# Revit family: Hager-Type B SP&N Distribution Boards-Surface_mounted-IP3X-With_Cover-NoHosted-GB-en
name_source: partatom
category: Electrical Equipment
units: mm (PartAtom-declared; Revit-internal decimal feet)

## family parameters
Always vertical = Yes
Cut with Voids When Loaded = No
Maintain Annotation Orientation = No
Panel Configuration = Two Columns, Circuits Across
Part Type = Panelboard
Room Calculation Point = No
Round Connector Dimension = Use Diameter
Shared = No
Work Plane-Based = Yes

## types (42) — shared parameters
BC_MODEL_ID = 1554493
BC_OBJECT_ID = 513945
BC_OBJECT_VERSION = #1
Classification.Uniclass.Pr.Description = Control circuit device enclosures
Classification.Uniclass.Pr.Number = Pr_80_77_28_16
Code hager = ADD-EC000214_UKVR
Default Elevation = 1219 mm
EF000003 - Mounting method = Surface mounted
EF000007 - Colour = Grey
EF000008 - Width = 465 mm  [stored 1.52559 ft]
EF000024 - UV resistant = No
EF000116 - RAL number = 7035
EF000118 - With mounting plate = No
EF000218 - Built-in depth = 150 mm
EF000332 - Built-in height = 450 mm  [stored 1.47638 ft]
EF000846 - Built-in width = 350 mm  [stored 1.14829 ft]
EF001062 - EMC-version = No
EF001088 - Extension possible = Yes
EF001134 - DIN-rail = Yes
EF001134 - With DIN-rail = No
EF001596 - Housing material = Steel
EF005474 - Degree of protection (IP rating) = IP3X
EF006306 - With lock = Yes
EF015776 - Earthing terminal block = Yes
EF015777 - Neutral terminal block = Yes
EF015941 - Signal passing door = No
ETIM class code = EC000214
ETIM class name = Small distribution board
HG000002-With door or cover = Yes
HG000003-Range = Type B SP&N Distribution Boards
HG000005-Thickness = 3 mm  [stored 0.00984252 ft]
HG000006-Flush mounted = No
HG000017-Distance between poles = 18 mm  [stored 0.0590551 ft]
HG000060-RAL-number = 7035
HG000099-Onfly Template ID = 507572
Manufacturer = Hager
Name = Type B SP&N Distribution Boards-Surface_mounted-IP3X-With_Cover-GB
Name BIM&CO = Electricity
Name hager = ADD_Enclosures_EC000214
Type Comments = Type B SP&N Distribution Boards
Uniformat = Low Tension Service & Dist.
Uniformat code = D501001
zero-valued in all types: EF000218 - Recess depth, EF000266 - Number of rows, EF000332 - Recess height, EF000846 - Recess width, EF001131 - Internal depth

## per-type parameters (varying)
| type | BC_VARIANT_ID | EF000040 - Height | EF000049 - Depth | EF002950 - Width in number of modular spacings | EF006244 - Transparent cover/door | HG000004-Manufacturer reference | HGEF000266-Number of rows | HGEF002950-Width in number of modular spacings | Model |
| Type B SP&N Distribution Boards-Surface_mounted_W465_H500_D132_6_Modular_Spacing-JK104B | 1179296 | 500 mm  [stored 1.64042 ft] | 132 mm  [stored 0.433071 ft] | 6 | No | JK104B | 0 | 8 | JK104B |
| Type B SP&N Distribution Boards-Surface_mounted_W465_H500_D132_6_Modular_Spacing-JK104BA3 | 1179297 | 500 mm  [stored 1.64042 ft] | 132 mm  [stored 0.433071 ft] | 6 | No | JK104BA3 | 0 | 12 | JK104BA3 |
| Type B SP&N Distribution Boards-Surface_mounted_W465_H500_D132_6_Modular_Spacing-JK104BG | 1179298 | 500 mm  [stored 1.64042 ft] | 132 mm  [stored 0.433071 ft] | 6 | Yes | JK104BG | 0 | 16 | JK104BG |
| Type B SP&N Distribution Boards-Surface_mounted_W465_H550_D132_9_Modular_Spacing-JK106B | 1179299 | 550 mm | 132 mm  [stored 0.433071 ft] | 9 | Yes | JK106B | 0 | 22 | JK106B |
| Type B SP&N Distribution Boards-Surface_mounted_W465_H550_D132_9_Modular_Spacing-JK106BA3 | 1179300 | 550 mm | 132 mm  [stored 0.433071 ft] | 9 | No | JK106BA3 | 0 | 12 | JK106BA3 |
| Type B SP&N Distribution Boards-Surface_mounted_W465_H550_D132_9_Modular_Spacing-JK106BG | 1179301 | 550 mm | 132 mm  [stored 0.433071 ft] | 9 | Yes | JK106BG | 0 | 16 | JK106BG |
| Type B SP&N Distribution Boards-Surface_mounted_W465_H625_D132_12_Modular_Spacing-JK108B | 1179302 | 625 mm  [stored 2.05052 ft] | 132 mm  [stored 0.433071 ft] | 12 | No | JK108B | 0 | 22 | JK108B |
| Type B SP&N Distribution Boards-Surface_mounted_W465_H625_D132_12_Modular_Spacing-JK108BA3 | 1179303 | 625 mm  [stored 2.05052 ft] | 132 mm  [stored 0.433071 ft] | 12 | No | JK108BA3 | 0 | 22 | JK108BA3 |
| Type B SP&N Distribution Boards-Surface_mounted_W465_H625_D132_12_Modular_Spacing-JK108BG | 1179304 | 625 mm  [stored 2.05052 ft] | 132 mm  [stored 0.433071 ft] | 12 | Yes | JK108BG | 0 | 16 | JK108BG |
| Type B SP&N Distribution Boards-Surface_mounted_W465_H850_D132_18_Modular_Spacing-JK112B | 1179305 | 850 mm  [stored 2.78871 ft] | 132 mm  [stored 0.433071 ft] | 18 | No | JK112B | 0 | 22 | JK112B |
| Type B SP&N Distribution Boards-Surface_mounted_W465_H850_D132_18_Modular_Spacing-JK112BA3 | 1179306 | 850 mm  [stored 2.78871 ft] | 132 mm  [stored 0.433071 ft] | 18 | No | JK112BA3 | 0 | 22 | JK112BA3 |
| Type B SP&N Distribution Boards-Surface_mounted_W465_H850_D132_18_Modular_Spacing-JK112BG | 1179307 | 850 mm  [stored 2.78871 ft] | 132 mm  [stored 0.433071 ft] | 18 | Yes | JK112BG | 1 | 16 | JK112BG |
| Type B SP&N Distribution Boards-Surface_mounted_W465_H950_D132_24_Modular_Spacing-JK116B | 1179308 | 950 mm  [stored 3.1168 ft] | 132 mm  [stored 0.433071 ft] | 24 | No | JK116B | 0 | 0 | JK116B |
| Type B SP&N Distribution Boards-Surface_mounted_W465_H950_D132_24_Modular_Spacing-JK116BA3 | 1179309 | 950 mm  [stored 3.1168 ft] | 132 mm  [stored 0.433071 ft] | 24 | No | JK116BA3 | 0 | 0 | JK116BA3 |
| Type B SP&N Distribution Boards-Surface_mounted_W465_H950_D132_24_Modular_Spacing-JK116BG | 1179310 | 950 mm  [stored 3.1168 ft] | 132 mm  [stored 0.433071 ft] | 24 | Yes | JK116BG | 0 | 0 | JK116BG |
| Type B SP&N Distribution Boards-Surface_mounted_W465_H1100_D165_27_Modular_Spacing-JK118B | 1179311 | 1100 mm | 165 mm | 27 | No | JK118B | 0 | 0 | JK118B |
| Type B SP&N Distribution Boards-Surface_mounted_W465_H1100_D165_27_Modular_Spacing-JK118BA3 | 1179312 | 1100 mm | 165 mm | 27 | No | JK118BA3 | 0 | 0 | JK118BA3 |
| Type B SP&N Distribution Boards-Surface_mounted_W465_H1100_D165_27_Modular_Spacing-JK118BG | 1179313 | 1100 mm | 165 mm | 27 | Yes | JK118BG | 0 | 0 | JK118BG |
| Type B SP&N Distribution Boards-Surface_mounted_W465_H1250_D165_36_Modular_Spacing-JK124B | 1179314 | 1250 mm  [stored 4.10105 ft] | 165 mm | 36 | No | JK124B | 1 | 16 | JK124B |
| Type B SP&N Distribution Boards-Surface_mounted_W465_H1250_D165_36_Modular_Spacing-JK124BA3 | 1179315 | 1250 mm  [stored 4.10105 ft] | 165 mm | 36 | No | JK124BA3 | 1 | 16 | JK124BA3 |
| Type B SP&N Distribution Boards-Surface_mounted_W465_H1250_D165_36_Modular_Spacing-JK124BG | 1179316 | 1250 mm  [stored 4.10105 ft] | 165 mm | 36 | Yes | JK124BG | 2 | 16 | JK124BG |
| Type B SP&N Distribution Boards-Surface_mounted_W465_H1250_D165_18_Modular_Spacing-JK20210B | 1179317 | 1250 mm  [stored 4.10105 ft] | 165 mm | 18 | No | JK20210B | 2 | 16 | JK20210B |
| Type B SP&N Distribution Boards-Surface_mounted_W465_H1250_D165_18_Modular_Spacing-JK20210BG | 1179318 | 1250 mm  [stored 4.10105 ft] | 165 mm | 18 | Yes | JK20210BG | 2 | 16 | JK20210BG |
| Type B SP&N Distribution Boards-Surface_mounted_W465_H1400_D165_27_Modular_Spacing-JK20216B | 1179319 | 1400 mm  [stored 4.59318 ft] | 165 mm | 27 | No | JK20216B | 2 | 16 | JK20216B |
| Type B SP&N Distribution Boards-Surface_mounted_W465_H1400_D165_27_Modular_Spacing-JK20216BG | 1179320 | 1400 mm  [stored 4.59318 ft] | 165 mm | 27 | Yes | JK20216BG | 2 | 16 | JK20216BG |
| Type B SP&N Distribution Boards-Surface_mounted_W465_H1400_D165_33_Modular_Spacing-JK20220B | 1179321 | 1400 mm  [stored 4.59318 ft] | 165 mm | 33 | No | JK20220B | 2 | 16 | JK20220B |
| Type B SP&N Distribution Boards-Surface_mounted_W465_H1400_D165_33_Modular_Spacing-JK20220BG | 1179322 | 1400 mm  [stored 4.59318 ft] | 165 mm | 33 | Yes | JK20220BG | 3 | 16 | JK20220BG |
| Type B SP&N Distribution Boards-Surface_mounted_W465_H950_D166_12_Modular_Spacing-JK208B | 1179323 | 950 mm  [stored 3.1168 ft] | 166 mm  [stored 0.544619 ft] | 12 | No | JK208B | 3 | 16 | JK208B |
| Type B SP&N Distribution Boards-Surface_mounted_W465_H950_D165_12_Modular_Spacing-JK208BA3 | 1179324 | 950 mm  [stored 3.1168 ft] | 165 mm | 12 | No | JK208BA3 | 4 | 16 | JK208BA3 |
| Type B SP&N Distribution Boards-Surface_mounted_W465_H950_D165_12_Modular_Spacing-JK208BG | 1179325 | 950 mm  [stored 3.1168 ft] | 165 mm | 12 | Yes | JK208BG | 4 | 16 | JK208BG |
| Type B SP&N Distribution Boards-Surface_mounted_W465_H1100_D165_18_Modular_Spacing-JK212B | 1179326 | 1100 mm | 165 mm | 18 | No | JK212B | 5 | 16 | JK212B |
| Type B SP&N Distribution Boards-Surface_mounted_W465_H1100_D165_18_Modular_Spacing-JK212BA3 | 1179327 | 1100 mm | 165 mm | 18 | No | JK212BA3 | 5 | 16 | JK212BA3 |
| Type B SP&N Distribution Boards-Surface_mounted_W465_H1100_D165_18_Modular_Spacing-JK212BG | 1179328 | 1100 mm | 165 mm | 18 | Yes | JK212BG | 1 | 16 | JK212BG |
| Type B SP&N Distribution Boards-Surface_mounted_W465_H1250_D165_24_Modular_Spacing-JK216B | 1179329 | 1250 mm  [stored 4.10105 ft] | 165 mm | 24 | No | JK216B | 5 | 16 | JK216B |
| Type B SP&N Distribution Boards-Surface_mounted_W465_H1250_D166_24_Modular_Spacing-JK216BA3 | 1179330 | 1250 mm  [stored 4.10105 ft] | 166 mm  [stored 0.544619 ft] | 24 | No | JK216BA3 | 5 | 16 | JK216BA3 |
| Type B SP&N Distribution Boards-Surface_mounted_W465_H1250_D165_24_Modular_Spacing-JK216BG | 1179331 | 1250 mm  [stored 4.10105 ft] | 165 mm | 24 | Yes | JK216BG | 5 | 16 | JK216BG |
| Type B SP&N Distribution Boards-Surface_mounted_W465_H1400_D165_27_Modular_Spacing-JK218B | 1179332 | 1400 mm  [stored 4.59318 ft] | 165 mm | 27 | No | JK218B | 5 | 16 | JK218B |
| Type B SP&N Distribution Boards-Surface_mounted_W465_H1400_D166_27_Modular_Spacing-JK218BA3 | 1179333 | 1400 mm  [stored 4.59318 ft] | 166 mm  [stored 0.544619 ft] | 27 | No | JK218BA3 | 6 | 16 | JK218BA3 |
| Type B SP&N Distribution Boards-Surface_mounted_W465_H1400_D165_27_Modular_Spacing-JK218BG | 1179334 | 1400 mm  [stored 4.59318 ft] | 165 mm | 27 | Yes | JK218BG | 6 | 16 | JK218BG |
| Type B SP&N Distribution Boards-Surface_mounted_W465_H1550_D165_36_Modular_Spacing-JK224B | 1179335 | 1550 mm  [stored 5.0853 ft] | 165 mm | 36 | No | JK224B | 1 | 16 | JK224B |
| Type B SP&N Distribution Boards-Surface_mounted_W465_H1550_D165_36_Modular_Spacing-JK224BA3 | 1179336 | 1550 mm  [stored 5.0853 ft] | 165 mm | 36 | No | JK224BA3 | 1 | 16 | JK224BA3 |
| Type B SP&N Distribution Boards-Surface_mounted_W465_H1550_D165_36_Modular_Spacing-JK224BG | 1179337 | 1550 mm  [stored 5.0853 ft] | 165 mm | 36 | Yes | JK224BG | 7 | 16 | JK224BG |

note: column(s) folded — value = type name in every type: Reference

note: [stored X ft] marks values corroborated as IEEE doubles in the binary element streams (Revit-internal decimal feet)

## geometry (parser evidence)
native form markers: Sweep x11
no freeform markers — native parametric forms only
